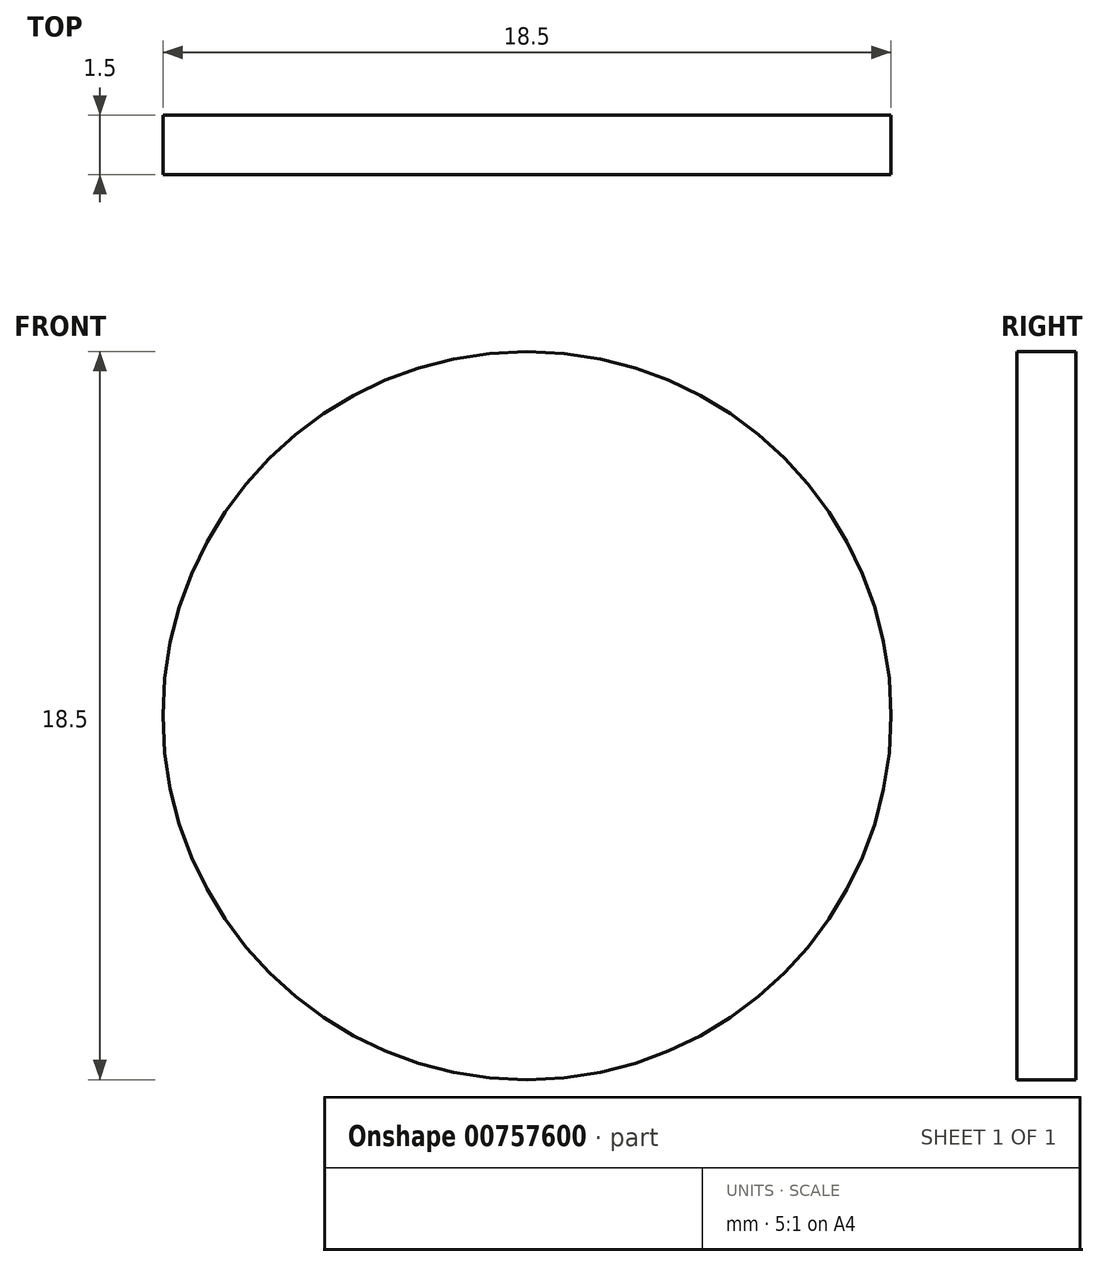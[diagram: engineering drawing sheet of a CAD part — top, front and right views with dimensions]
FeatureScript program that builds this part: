
annotation { "Feature Type Name" : "Feature", "Feature Type Description" : "" }
export const myFeature = defineFeature(function(context is Context, id is Id, definition is map)
    precondition{}
    {
        {
            var Q0;
            Q0=qCreatedBy(makeId("Front.planeOp"),FACE);
            var sketch = newSketch(context, id + "F0", { "sketchPlane" : qUnion([Q0])});
            skCircle(sketch, "E0", {"center": v(0, 0) * mm, "radius": 9.25 * mm});
            skSolve(sketch);
        }
        {
            var Q0;
            Q0 = qSketchRegion(id + "F0", true);
            extrude(context, id + "F1", {"entities" : qUnion([Q0]), "depth" : 1.5 * mm, "offsetDistance" : 25 * mm});
        }
    });
